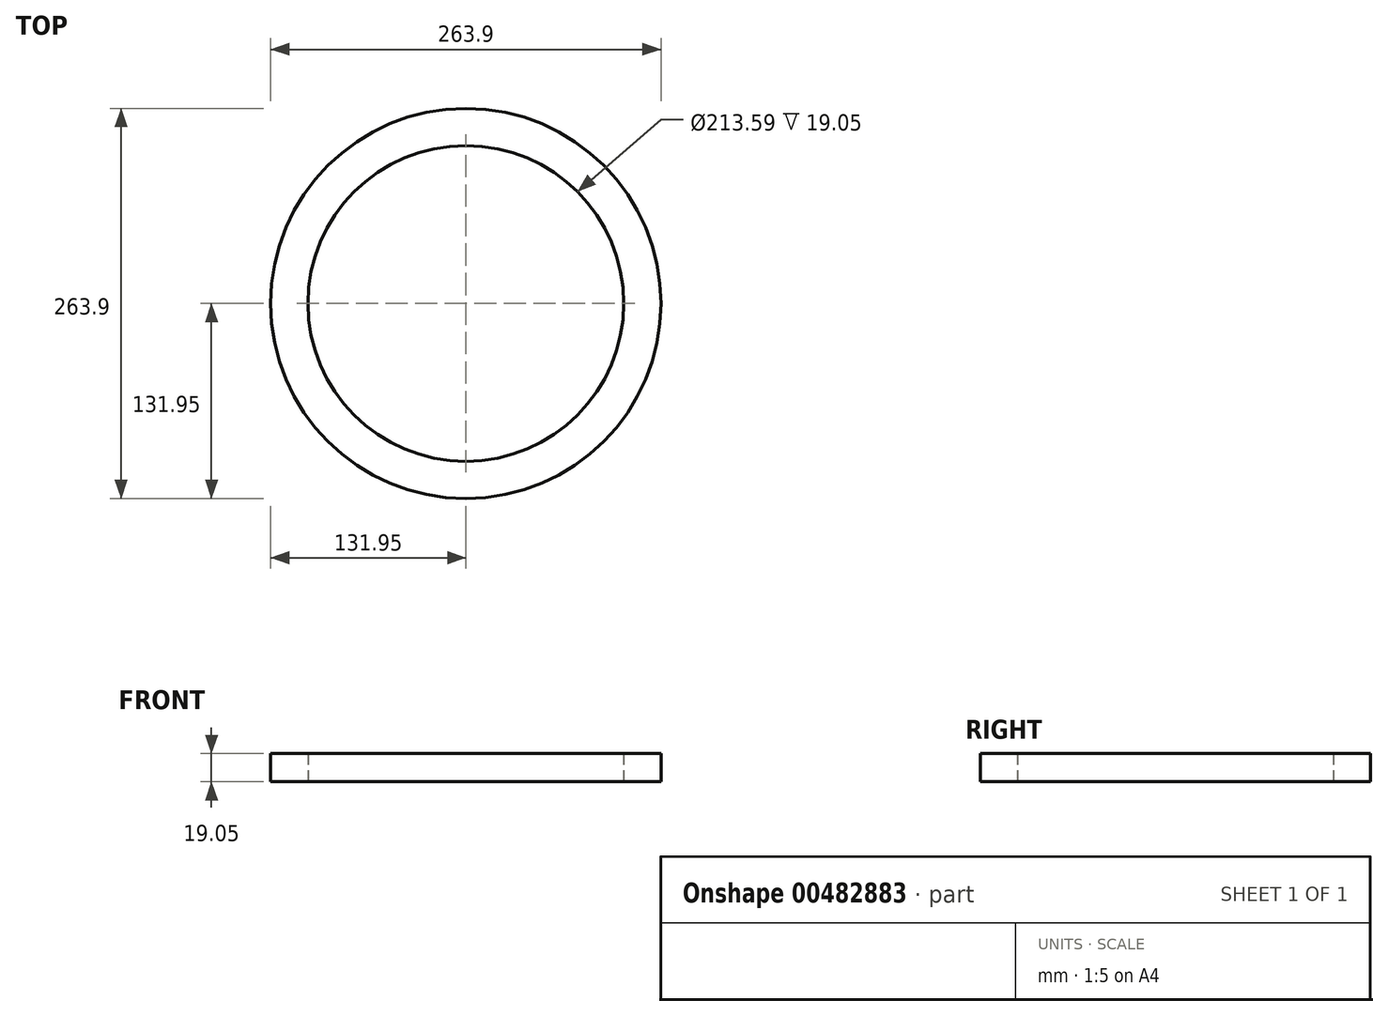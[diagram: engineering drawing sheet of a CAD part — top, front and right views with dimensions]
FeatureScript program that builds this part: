
annotation { "Feature Type Name" : "Feature", "Feature Type Description" : "" }
export const myFeature = defineFeature(function(context is Context, id is Id, definition is map)
    precondition{}
    {
        {
            var Q0;
            Q0=qCreatedBy(makeId("Top.planeOp"),FACE);
            var sketch = newSketch(context, id + "F0", { "sketchPlane" : qUnion([Q0])});
            skCircle(sketch, "E0", {"center": v(0, 0) * mm, "radius": 131.95 * mm});
            skCircle(sketch, "E1", {"center": v(0, 0) * mm, "radius": 106.8 * mm});
            skSolve(sketch);
        }
        {
            var Q0;
            Q0 = qSketchRegion(id + "F0", true);
            var Q1;
            {var subQ0=sQuery(id+"F0.wireOp",EDGE,"Zm1uzvQB-yDc6-zx3K-eE32-99IJRzujL7Iz");Q1=makeQuery(id+"F0.imprint","IMPRINT",FACE,{"disambiguationData":[TD([[makeQuery(id+"F0.imprint","IMPRINT",EDGE,{"derivedFrom":subQ0}),-1.0]])]});}
            extrude(context, id + "F1", {"entities" : qUnion([Q0, Q1]), "depth" : 19.05 * mm, "offsetDistance" : 25.4 * mm});
        }
    });
